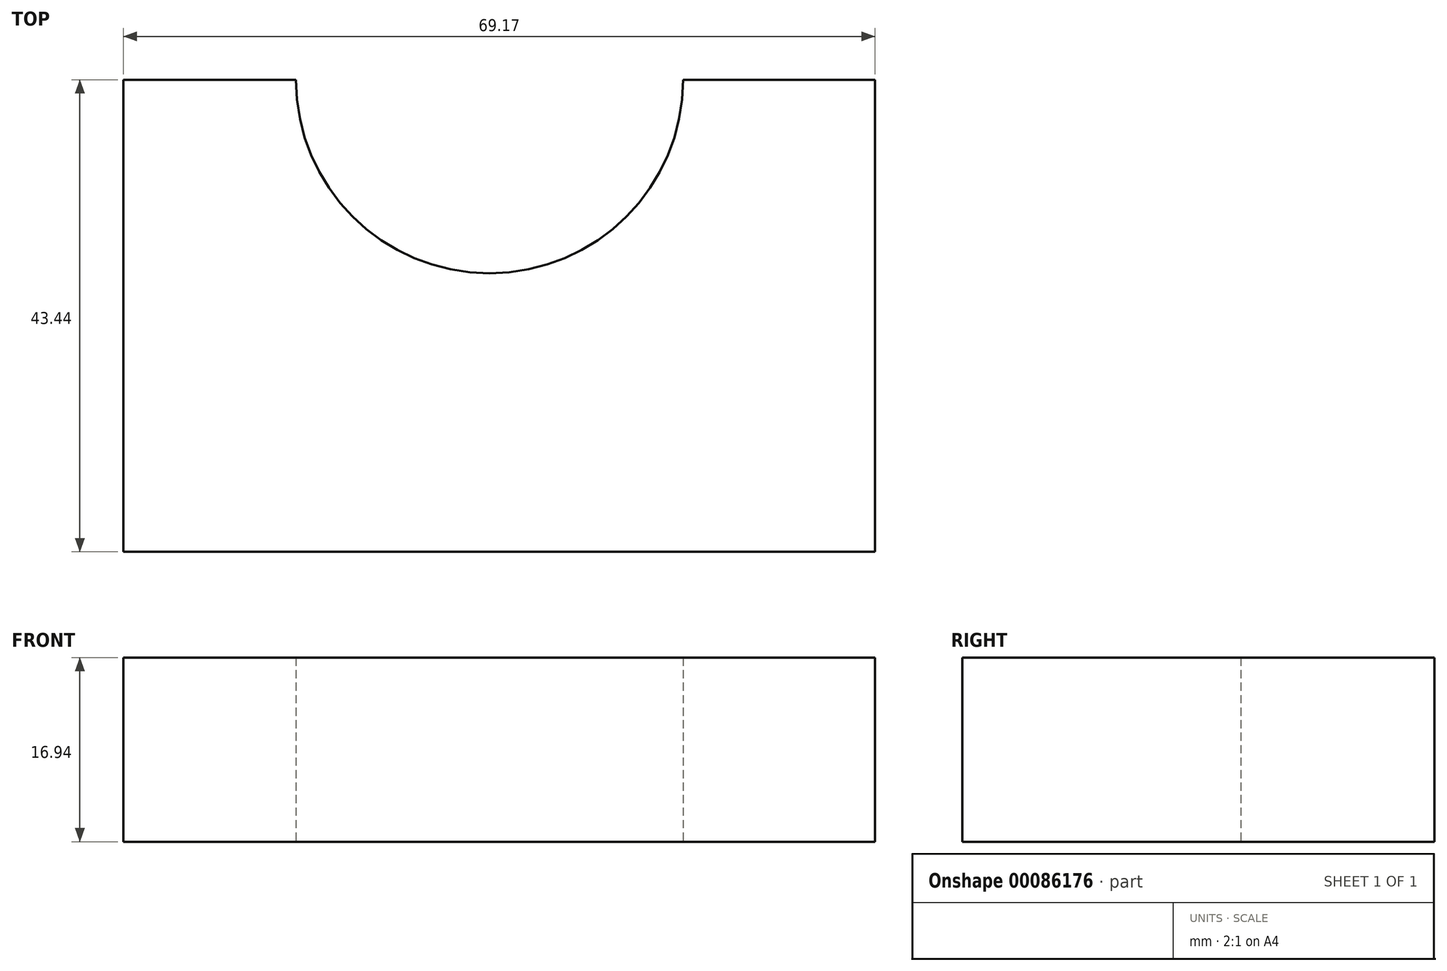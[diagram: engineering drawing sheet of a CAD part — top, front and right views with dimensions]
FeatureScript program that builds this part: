
annotation { "Feature Type Name" : "Feature", "Feature Type Description" : "" }
export const myFeature = defineFeature(function(context is Context, id is Id, definition is map)
    precondition{}
    {
        {
            var Q0;
            Q0=qCreatedBy(makeId("Top.planeOp"),FACE);
            var sketch = newSketch(context, id + "F0", { "sketchPlane" : qUnion([Q0])});
            skLineSegment(sketch, "E0.bottom", {"start": v(-31.93, 27.52) * mm, "end": v(37.24, 27.52) * mm});
            skLineSegment(sketch, "E0.top", {"start": v(-31.93, -15.92) * mm, "end": v(37.24, -15.92) * mm});
            skLineSegment(sketch, "E0.left", {"start": v(-31.93, 27.52) * mm, "end": v(-31.93, -15.92) * mm});
            skLineSegment(sketch, "E0.right", {"start": v(37.24, 27.52) * mm, "end": v(37.24, -15.92) * mm});
            skCircle(sketch, "E1", {"center": v(1.76, 27.52) * mm, "radius": 17.8 * mm});
            skSolve(sketch);
        }
        {
            var Q0;
            Q0=makeQuery(id+"F0.imprint","IMPRINT",FACE,{"disambiguationData":[TD([[makeQuery(id+"F0.imprint","IMPRINT",EDGE,{"derivedFrom":sQuery(id+"F0.wireOp",EDGE,"E0.top")}),1.0]])]});
            extrude(context, id + "F1", {"entities" : qUnion([Q0]), "depth" : 16.94 * mm});
        }
    });
